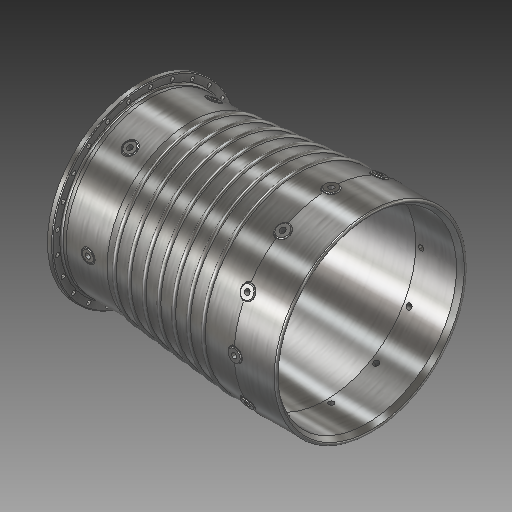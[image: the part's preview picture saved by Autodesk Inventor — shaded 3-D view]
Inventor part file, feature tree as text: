
AUTODESK INVENTOR PART (.ipt)
format: ipt  version: 2019 (Build 230136000, 136)  size: 1,079,808 bytes
history: native  units: in
note: dims shown in document units (in); Inventor stores cm internally (conversion verified against a paired STEP export)
features: sketch x5, fillet x4, hole x3, pattern_circular x3, revolve x2, plane x2, extrude x2
ambient origin geometry x8: Origin, YZ Plane, XZ Plane, XY Plane, X Axis, Y Axis, Z Axis, Center Point
bodies: Solid1 (feature_tree)
feature tree (21):
  revolve  "Revolution1"  [1 undecoded]
  hole  "Hole1"  [1 undecoded]
  pattern_circular  "Circular Pattern1"  Angle=90.0deg  [1 undecoded]
  plane  "Work Plane1"
  extrude  "Extrusion1"  Depth=0.0787in
  hole  "Hole2"  [1 undecoded]
  fillet  "Fillet1"  Radius=9.8425in
  fillet  "Fillet2"  Radius=0.5709in
  pattern_circular  "Circular Pattern2"  [2 undecoded]
  plane  "Work Plane2"
  extrude  "Extrusion2"  Depth=0.0787in
  fillet  "Fillet3"  Radius=0.3937in
  hole  "Hole3"  [1 undecoded]
  pattern_circular  "Circular Pattern3"  [2 undecoded]
  revolve  "Revolution2"  [1 undecoded]
  fillet  "Fillet4"  Radius=2.3622in
  sketch  "Sketch1"  dims[d1=0.7611in d2=0.0394in]
  sketch  "Sketch2"  dims[d3=0.0787in d4=8.9565in]
  sketch  "Sketch3"  dims[d5=1.8641in]
  sketch  "Sketch4"  dims[d6=7.5197in]
  sketch  "Sketch5"  dims[d7=0.2853in d15=90.0deg d16=4.252in d17=0.2126in d18=0.2126in d19=0.2362in d20=0.1575in d21=0.0787in d22=90.0deg d23=0.315in d24=0.8108in d25=9.8425in d26=360.0deg d28=0.5709in d29=1.5354in d30=4.0611in d31=0.3937in d32=0.0in d33=0.3937in d34=0.3937in d35=0.2559in d36=0.2362in d37=0.1575in d38=0.0787in d39=90.0deg d40=1.69in d41=0.8108in d42=0.0787in d43=0.0787in d44=2.3622in d45=360.0deg d51=1.9685in d52=1.2712in d56=1.9685in d57=2.1654in d58=8.6614in d59=0.3937in d60=0.6693in d62=0.0591in d63=0.0787in d64=0.0in d65=0.0in d66=0.0394in d76=0.3937in d77=0.3937in d69=0.2559in d70=0.2362in d71=0.1575in d72=0.0787in d73=90.0deg d74=0.3937in d75=0.8108in d78=4.7244in d79=360.0deg d81=7.6935in d82=0.1969in d83=0.3937in d84=2.7559in d86=0.7874in d87=0.3937in d89=0.3937in d91=90.0deg d92=0.0787in d102=9.4698in]
note: 10 required parameter values undecoded (feature->parameter linkage not recoverable at this tier; creation-order binding heuristic only, values carry confidence <= 0.55)